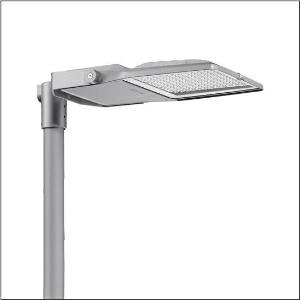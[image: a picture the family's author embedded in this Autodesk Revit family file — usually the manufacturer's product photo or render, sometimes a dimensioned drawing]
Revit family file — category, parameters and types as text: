
# Revit family: floodlight_fl_21_iq_midi___pl33t_5xa7781f2f3a_a5b2
name_source: partatom
category: Lighting Fixtures
units: mm (PartAtom-declared; Revit-internal decimal feet)

## family parameters
Cut with Voids When Loaded = No
Host = Face
Light Source = No
Part Type = Normal
Room Calculation Point = No
Round Connector Dimension = Use Diameter
Shared = No

## types (1)
- --- (1 x LED, 35350 lm, 270.2 W, 3000K)
    Apparent Load = 270 VA
    CIE Flux Codes = 26 75 99 100 100
    Color Rendering = 70
    Color Temperature = 3000K
    Default Elevation = 1800 mm
    Description = Floodlight FL 21 iQ midi, floodlight, primary light control with lens, of PMMA, primary optical cover: protective disc, of toughened safety glass, transparent, light distribution: PL33T, light emission: direct distribution, installation type: surface-mounted, LED, High Power LED, rated luminous flux: 35.350lm, luminous efficacy: 131lm/W, light colour: 730, colour temperature: 3000K, control gear: ECG iQ, control: optimised constant luminous flux control (CLO 2.0), Desk-Remote (wireless, voltage-free reading and setting of iQ features in the workshop via application-optimized NFC function/RFID function), Light-Fading, Smart-Wire, Night-Set, Lumen-Switch, Temp-Guard, Auto-Match, with terminal, 6-pole, mains connection: 220..240V, AC, 50/60Hz, start of lifetime: 270W, end of service life: 287W, reduction: 117W, luminaire housing, of diecast aluminium, powder-coated, Siteco® metallic grey (DB 702S), corrosivity category C5 mid according to DIN EN ISO 12944, sealing non-destructively replaceable, please order mast flange separately, mast bracket, of steel, galvanised, powder-coated, Siteco® metallic grey (DB 702S), protection rating (complete): IP66, insulation class (complete): insulation class II (safety insulation), certification: CE, protection symbol: D, impact resistance: IK08, permissible operating ambient temperature: -40..+40°C, permissible operating ambient temperature for outdoor applications: -40..+50°C, standard: DIN EN 12944, LABS conformity tested according to VDMA 24364:2018-05, packaging unit: 1 piece

Light Distribution: PL33T
    Height = 76 mm
    Lamp = 1 x LED
    Lamp Light Flux = 35350 lm
    Lamp Power = 270.2 W
    Lamp count = 1
    Length = 657 mm
    Luminous efficacy = 131 lm/W
    Manufacturer = Siteco
    ModVariant = No
    Model = 5XA7781F2F3A
    Number of Poles = 1
    OnlyDefault = Yes
    Power Factor = 1
    Product Name = Floodlight FL 21 iQ midi | PL33T
    Product group = floodlight | pylon annexe
    ProductGroupID = 6200
    Protection Class = Protection class II
    Protection Degree = IP 66
    RLX_Detail_Level = 1
    RLX_Emergency_Light_Flux = 0 lm
    RLX_Emergency_Type = 0
    RLX_Emergency_Type_DB = No
    RlxData = <blob elided: 153577 chars, md5=a28720ef>
    Socket = socket
    Standby Power = 0 W
    System Light Flux = 35350 lm
    System Power = 270 W
    Type Comments = factory setting: luminous flux: 100 % | dim-lin: 254 | 620 mA
    Type Image = l_1007123.jpg
    URL = http://relux.com
    VarID = @adj_033691
    Voltage = 0 V
    Weight = 0.00 kg
    Width = 442 mm

## geometry (parser evidence)
native form markers: Blend x4, Sweep x12
no freeform markers — native parametric forms only
